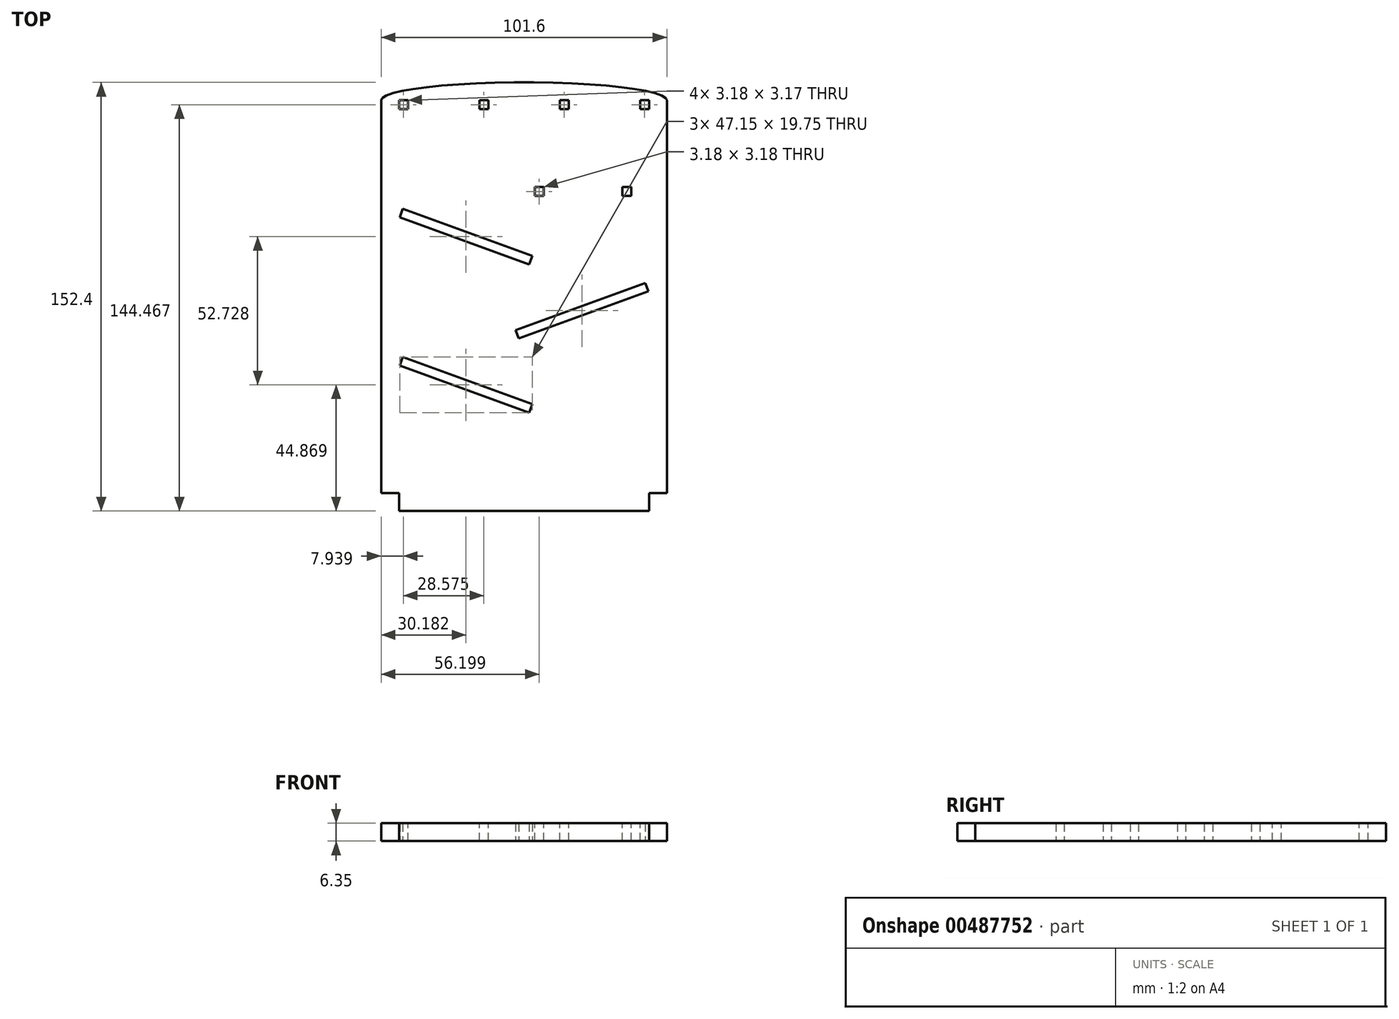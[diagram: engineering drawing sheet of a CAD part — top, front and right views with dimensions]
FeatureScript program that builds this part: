
annotation { "Feature Type Name" : "Feature", "Feature Type Description" : "" }
export const myFeature = defineFeature(function(context is Context, id is Id, definition is map)
    precondition{}
    {
        {
            var Q0;
            Q0=qCreatedBy(makeId("Top.planeOp"),FACE);
            var sketch = newSketch(context, id + "F0", { "sketchPlane" : qUnion([Q0])});
            skLineSegment(sketch, "E0.bottom", {"start": v(-69.59, 73.12) * mm, "end": v(32.01, 73.12) * mm});
            skLineSegment(sketch, "E0.top", {"start": v(-69.59, -72.93) * mm, "end": v(32.01, -72.93) * mm});
            skLineSegment(sketch, "E0.left", {"start": v(-69.59, 73.12) * mm, "end": v(-69.59, -72.93) * mm});
            skLineSegment(sketch, "E0.right", {"start": v(32.01, 73.12) * mm, "end": v(32.01, -72.93) * mm});
            skSolve(sketch);
        }
        {
            var Q0;
            Q0 = qSketchRegion(id + "F0", true);
            extrude(context, id + "F1", {"entities" : qUnion([Q0]), "depth" : 6.35 * mm});
        }
        {
            var Q0;
            Q0=makeQuery(id+"F1.opExtrude","CAP_FACE",FACE,{"disambiguationData":[OSD([sQuery(id+"F0.wireOp",EDGE,"E0.bottom"),sQuery(id+"F0.wireOp",EDGE,"E0.top"),sQuery(id+"F0.wireOp",EDGE,"E0.left"),sQuery(id+"F0.wireOp",EDGE,"E0.right")])],"isStart":false});
            var sketch = newSketch(context, id + "F2", { "sketchPlane" : qUnion([Q0])});
            skPoint(sketch, "E1.oppositeSnap0", {"position": v(-18.79, 73.12) * mm});
            skLineSegment(sketch, "E1.bottom", {"start": v(-69.59, 73.12) * mm, "end": v(-18.79, 73.12) * mm});
            skLineSegment(sketch, "E1.top", {"start": v(-69.59, 79.47) * mm, "end": v(-18.79, 79.47) * mm});
            skLineSegment(sketch, "E1.left", {"start": v(-69.59, 73.12) * mm, "end": v(-69.59, 79.47) * mm});
            skLineSegment(sketch, "E1.right", {"start": v(-18.79, 73.12) * mm, "end": v(-18.79, 79.47) * mm});
            skLineSegment(sketch, "E2.bottom", {"start": v(-18.79, 79.47) * mm, "end": v(32.01, 79.47) * mm});
            skLineSegment(sketch, "E2.top", {"start": v(-18.79, 73.12) * mm, "end": v(32.01, 73.12) * mm});
            skLineSegment(sketch, "E2.left", {"start": v(-18.79, 79.47) * mm, "end": v(-18.79, 73.12) * mm});
            skLineSegment(sketch, "E2.right", {"start": v(32.01, 79.47) * mm, "end": v(32.01, 73.12) * mm});
            skEllipse(sketch, "E3", {"center": v(-18.79, 73.12) * mm, "majorRadius": 50.8 * mm, "minorRadius": 6.35 * mm, "majorAxis": v(-1, 0)});
            skSolve(sketch);
        }
        {
            var Q0;
            {var subQ0=sQuery(id+"F2.wireOp",EDGE,"E1.bottom");Q0=makeQuery(id+"F2.imprint","IMPRINT",FACE,{"disambiguationData":[TD([[makeQuery(id+"F2.imprint","IMPRINT",EDGE,{"derivedFrom":subQ0}),1.0]])]});}
            var Q1;
            {var subQ0=sQuery(id+"F2.wireOp",EDGE,"E2.top");Q1=makeQuery(id+"F2.imprint","IMPRINT",FACE,{"disambiguationData":[TD([[makeQuery(id+"F2.imprint","IMPRINT",EDGE,{"derivedFrom":subQ0}),1.0]])]});}
            extrude(context, id + "F3", {"entities" : qUnion([Q0, Q1]), "operationType" : NewBodyOperationType.ADD, "oppositeDirection" : true, "depth" : 6.35 * mm});
        }
        {
            var Q0;
            Q0=makeQuery(id+"F3.boolean.opBoolean","MERGE",FACE,{"derivedFrom":[makeQuery(id+"F1.opExtrude","CAP_FACE",FACE,{"disambiguationData":[OSD([sQuery(id+"F0.wireOp",EDGE,"E0.bottom"),sQuery(id+"F0.wireOp",EDGE,"E0.top"),sQuery(id+"F0.wireOp",EDGE,"E0.left"),sQuery(id+"F0.wireOp",EDGE,"E0.right")])],"isStart":false}),makeQuery(id+"F3.opExtrude","CAP_FACE",FACE,{"disambiguationData":[OSD([sQuery(id+"F2.wireOp",EDGE,"E1.bottom"),sQuery(id+"F2.wireOp",EDGE,"E2.top"),sQuery(id+"F2.wireOp",EDGE,"E3")])],"isStart":true})]});
            var sketch = newSketch(context, id + "F4", { "sketchPlane" : qUnion([Q0])});
            skLineSegment(sketch, "E4.bottom", {"start": v(-69.59, -72.93) * mm, "end": v(-63.24, -72.93) * mm});
            skLineSegment(sketch, "E4.top", {"start": v(-69.59, -66.58) * mm, "end": v(-63.24, -66.58) * mm});
            skLineSegment(sketch, "E4.left", {"start": v(-69.59, -72.93) * mm, "end": v(-69.59, -66.58) * mm});
            skLineSegment(sketch, "E4.right", {"start": v(-63.24, -72.93) * mm, "end": v(-63.24, -66.58) * mm});
            skLineSegment(sketch, "E5.bottom", {"start": v(32.01, -72.93) * mm, "end": v(25.66, -72.93) * mm});
            skLineSegment(sketch, "E5.top", {"start": v(32.01, -66.58) * mm, "end": v(25.66, -66.58) * mm});
            skLineSegment(sketch, "E5.left", {"start": v(32.01, -72.93) * mm, "end": v(32.01, -66.58) * mm});
            skLineSegment(sketch, "E5.right", {"start": v(25.66, -72.93) * mm, "end": v(25.66, -66.58) * mm});
            skLineSegment(sketch, "E6.bottom", {"start": v(-69.59, 73.12) * mm, "end": v(32.01, 73.12) * mm});
            skLineSegment(sketch, "E6.top", {"start": v(-69.59, 66.77) * mm, "end": v(32.01, 66.77) * mm});
            skLineSegment(sketch, "E6.left", {"start": v(-69.59, 73.12) * mm, "end": v(-69.59, 66.77) * mm});
            skLineSegment(sketch, "E6.right", {"start": v(32.01, 73.12) * mm, "end": v(32.01, 66.77) * mm});
            skLineSegment(sketch, "E7.bottom", {"start": v(-69.59, 66.77) * mm, "end": v(-63.24, 66.77) * mm});
            skLineSegment(sketch, "E8.bottom", {"start": v(32.01, 66.77) * mm, "end": v(25.66, 66.77) * mm});
            skLineSegment(sketch, "E9.bottom", {"start": v(-63.24, 66.77) * mm, "end": v(-69.59, 66.77) * mm});
            skLineSegment(sketch, "E9.top", {"start": v(-63.24, 73.12) * mm, "end": v(-69.59, 73.12) * mm});
            skLineSegment(sketch, "E9.left", {"start": v(-63.24, 66.77) * mm, "end": v(-63.24, 73.12) * mm});
            skLineSegment(sketch, "E9.right", {"start": v(-69.59, 66.77) * mm, "end": v(-69.59, 73.12) * mm});
            skLineSegment(sketch, "E10.bottom", {"start": v(25.66, 66.77) * mm, "end": v(32.01, 66.77) * mm});
            skLineSegment(sketch, "E10.top", {"start": v(25.66, 73.12) * mm, "end": v(32.01, 73.12) * mm});
            skLineSegment(sketch, "E10.left", {"start": v(25.66, 66.77) * mm, "end": v(25.66, 73.12) * mm});
            skLineSegment(sketch, "E10.right", {"start": v(32.01, 66.77) * mm, "end": v(32.01, 73.12) * mm});
            skSolve(sketch);
        }
        {
            var Q0;
            Q0=makeQuery(id+"F4.imprint","IMPRINT",FACE,{"disambiguationData":[TD([[makeQuery(id+"F4.imprint","IMPRINT",EDGE,{"derivedFrom":sQuery(id+"F4.wireOp",EDGE,"E9.bottom")}),-1.0]])]});
            var Q1;
            Q1=makeQuery(id+"F4.imprint","IMPRINT",FACE,{"disambiguationData":[TD([[makeQuery(id+"F4.imprint","IMPRINT",EDGE,{"derivedFrom":sQuery(id+"F4.wireOp",EDGE,"E10.bottom")}),1.0]])]});
            var Q2;
            Q2=makeQuery(id+"F4.imprint","IMPRINT",FACE,{"disambiguationData":[TD([[makeQuery(id+"F4.imprint","IMPRINT",EDGE,{"derivedFrom":sQuery(id+"F4.wireOp",EDGE,"E5.bottom")}),1.0]])]});
            var Q3;
            Q3=makeQuery(id+"F4.imprint","IMPRINT",FACE,{"disambiguationData":[TD([[makeQuery(id+"F4.imprint","IMPRINT",EDGE,{"derivedFrom":sQuery(id+"F4.wireOp",EDGE,"E4.bottom")}),1.0]])]});
            extrude(context, id + "F5", {"entities" : qUnion([Q0, Q1, Q2, Q3]), "operationType" : NewBodyOperationType.REMOVE, "endBound" : BoundingType.THROUGH_ALL, "oppositeDirection" : true, "depth" : 25.4 * mm});
        }
        {
            var Q0;
            Q0=makeQuery(id+"F3.boolean.opBoolean","MERGE",FACE,{"derivedFrom":[makeQuery(id+"F1.opExtrude","CAP_FACE",FACE,{"disambiguationData":[OSD([sQuery(id+"F0.wireOp",EDGE,"E0.bottom"),sQuery(id+"F0.wireOp",EDGE,"E0.top"),sQuery(id+"F0.wireOp",EDGE,"E0.left"),sQuery(id+"F0.wireOp",EDGE,"E0.right")])],"isStart":false}),makeQuery(id+"F3.opExtrude","CAP_FACE",FACE,{"disambiguationData":[OSD([sQuery(id+"F2.wireOp",EDGE,"E1.bottom"),sQuery(id+"F2.wireOp",EDGE,"E2.top"),sQuery(id+"F2.wireOp",EDGE,"E3")])],"isStart":true})]});
            var sketch = newSketch(context, id + "F6", { "sketchPlane" : qUnion([Q0])});
            skLineSegment(sketch, "E11.bottom", {"start": v(-63.24, 73.12) * mm, "end": v(-60.06, 73.12) * mm});
            skLineSegment(sketch, "E11.top", {"start": v(-63.24, 69.95) * mm, "end": v(-60.06, 69.95) * mm});
            skLineSegment(sketch, "E11.left", {"start": v(-63.24, 73.12) * mm, "end": v(-63.24, 69.95) * mm});
            skLineSegment(sketch, "E11.right", {"start": v(-60.06, 73.12) * mm, "end": v(-60.06, 69.95) * mm});
            skLineSegment(sketch, "E12.bottom", {"start": v(-34.66, 73.12) * mm, "end": v(-31.49, 73.12) * mm});
            skLineSegment(sketch, "E12.top", {"start": v(-34.66, 69.95) * mm, "end": v(-31.49, 69.95) * mm});
            skLineSegment(sketch, "E12.left", {"start": v(-34.66, 73.12) * mm, "end": v(-34.66, 69.95) * mm});
            skLineSegment(sketch, "E12.right", {"start": v(-31.49, 73.12) * mm, "end": v(-31.49, 69.95) * mm});
            skLineSegment(sketch, "E13.bottom", {"start": v(-6.09, 73.12) * mm, "end": v(-2.91, 73.12) * mm});
            skLineSegment(sketch, "E13.top", {"start": v(-6.09, 69.95) * mm, "end": v(-2.91, 69.95) * mm});
            skLineSegment(sketch, "E13.left", {"start": v(-6.09, 73.12) * mm, "end": v(-6.09, 69.95) * mm});
            skLineSegment(sketch, "E13.right", {"start": v(-2.91, 73.12) * mm, "end": v(-2.91, 69.95) * mm});
            skLineSegment(sketch, "E14.bottom", {"start": v(22.49, 73.12) * mm, "end": v(25.66, 73.12) * mm});
            skLineSegment(sketch, "E14.top", {"start": v(22.49, 69.95) * mm, "end": v(25.66, 69.95) * mm});
            skLineSegment(sketch, "E14.left", {"start": v(22.49, 73.12) * mm, "end": v(22.49, 69.95) * mm});
            skLineSegment(sketch, "E14.right", {"start": v(25.66, 73.12) * mm, "end": v(25.66, 69.95) * mm});
            skLineSegment(sketch, "E15", {"start": v(-11.8, 42.26) * mm, "end": v(16.14, 42.26) * mm});
            skLineSegment(sketch, "E16.bottom", {"start": v(-11.8, 42.26) * mm, "end": v(-14.98, 42.26) * mm});
            skLineSegment(sketch, "E16.top", {"start": v(-11.8, 39.09) * mm, "end": v(-14.98, 39.09) * mm});
            skLineSegment(sketch, "E16.left", {"start": v(-11.8, 42.26) * mm, "end": v(-11.8, 39.09) * mm});
            skLineSegment(sketch, "E16.right", {"start": v(-14.98, 42.26) * mm, "end": v(-14.98, 39.09) * mm});
            skLineSegment(sketch, "E17.bottom", {"start": v(16.14, 42.26) * mm, "end": v(19.31, 42.26) * mm});
            skLineSegment(sketch, "E17.top", {"start": v(16.14, 39.09) * mm, "end": v(19.31, 39.09) * mm});
            skLineSegment(sketch, "E17.left", {"start": v(16.14, 42.26) * mm, "end": v(16.14, 39.09) * mm});
            skLineSegment(sketch, "E17.right", {"start": v(19.31, 42.26) * mm, "end": v(19.31, 39.09) * mm});
            skLineSegment(sketch, "E18", {"start": v(-63.24, 73.12) * mm, "end": v(25.66, 73.12) * mm});
            skSolve(sketch);
        }
        {
            var Q0;
            Q0=makeQuery(id+"F6.imprint","IMPRINT",FACE,{"disambiguationData":[TD([[makeQuery(id+"F6.imprint","IMPRINT",EDGE,{"derivedFrom":sQuery(id+"F6.wireOp",EDGE,"E11.top")}),1.0]])]});
            var Q1;
            Q1=makeQuery(id+"F6.imprint","IMPRINT",FACE,{"disambiguationData":[TD([[makeQuery(id+"F6.imprint","IMPRINT",EDGE,{"derivedFrom":sQuery(id+"F6.wireOp",EDGE,"E12.top")}),1.0]])]});
            var Q2;
            Q2=makeQuery(id+"F6.imprint","IMPRINT",FACE,{"disambiguationData":[TD([[makeQuery(id+"F6.imprint","IMPRINT",EDGE,{"derivedFrom":sQuery(id+"F6.wireOp",EDGE,"E13.top")}),1.0]])]});
            var Q3;
            Q3=makeQuery(id+"F6.imprint","IMPRINT",FACE,{"disambiguationData":[TD([[makeQuery(id+"F6.imprint","IMPRINT",EDGE,{"derivedFrom":sQuery(id+"F6.wireOp",EDGE,"E14.top")}),1.0]])]});
            var Q4;
            Q4=makeQuery(id+"F6.imprint","IMPRINT",FACE,{"disambiguationData":[TD([[makeQuery(id+"F6.imprint","IMPRINT",EDGE,{"derivedFrom":sQuery(id+"F6.wireOp",EDGE,"E17.bottom")}),-1.0]])]});
            var Q5;
            Q5=makeQuery(id+"F6.imprint","IMPRINT",FACE,{"disambiguationData":[TD([[makeQuery(id+"F6.imprint","IMPRINT",EDGE,{"derivedFrom":sQuery(id+"F6.wireOp",EDGE,"E16.bottom")}),1.0]])]});
            extrude(context, id + "F7", {"entities" : qUnion([Q0, Q1, Q2, Q3, Q4, Q5]), "operationType" : NewBodyOperationType.REMOVE, "endBound" : BoundingType.THROUGH_ALL, "oppositeDirection" : true, "depth" : 25.4 * mm});
        }
        {
            var Q0;
            Q0=qCreatedBy(makeId("Top.planeOp"),FACE);
            var sketch = newSketch(context, id + "F8", { "sketchPlane" : qUnion([Q0])});
            skLineSegment(sketch, "E19", {"start": v(-62.98, 31.56) * mm, "end": v(-16.92, 14.8) * mm});
            skLineSegment(sketch, "E20", {"start": v(-62.98, 31.56) * mm, "end": v(-61.9, 34.54) * mm});
            skLineSegment(sketch, "E21", {"start": v(-61.9, 34.54) * mm, "end": v(-15.83, 17.77) * mm});
            skLineSegment(sketch, "E22", {"start": v(-15.83, 17.77) * mm, "end": v(-16.92, 14.8) * mm});
            skSolve(sketch);
        }
        {
            var Q0;
            Q0 = qSketchRegion(id + "F8", true);
            extrude(context, id + "F9", {"entities" : qUnion([Q0]), "operationType" : NewBodyOperationType.REMOVE, "depth" : 18.29 * mm});
        }
        {
            var Q0;
            Q0=qCreatedBy(makeId("Top.planeOp"),FACE);
            var sketch = newSketch(context, id + "F10", { "sketchPlane" : qUnion([Q0])});
            skLineSegment(sketch, "E23", {"start": v(-21.74, -8.59) * mm, "end": v(24.32, 8.18) * mm});
            skLineSegment(sketch, "E24", {"start": v(24.32, 8.18) * mm, "end": v(25.4, 5.2) * mm});
            skLineSegment(sketch, "E25", {"start": v(25.4, 5.2) * mm, "end": v(-20.66, -11.57) * mm});
            skLineSegment(sketch, "E26", {"start": v(-20.66, -11.57) * mm, "end": v(-21.74, -8.59) * mm});
            skSolve(sketch);
        }
        {
            var Q0;
            Q0 = qSketchRegion(id + "F10", true);
            extrude(context, id + "F11", {"entities" : qUnion([Q0]), "operationType" : NewBodyOperationType.REMOVE, "depth" : 25.65 * mm});
        }
        {
            var Q0;
            Q0=qCreatedBy(makeId("Top.planeOp"),FACE);
            var sketch = newSketch(context, id + "F12", { "sketchPlane" : qUnion([Q0])});
            skLineSegment(sketch, "E27", {"start": v(-61.9, -18.19) * mm, "end": v(-15.83, -34.95) * mm});
            skLineSegment(sketch, "E28", {"start": v(-15.83, -34.95) * mm, "end": v(-16.92, -37.94) * mm});
            skLineSegment(sketch, "E29", {"start": v(-16.92, -37.94) * mm, "end": v(-62.98, -21.17) * mm});
            skLineSegment(sketch, "E30", {"start": v(-62.98, -21.17) * mm, "end": v(-61.9, -18.19) * mm});
            skSolve(sketch);
        }
        {
            var Q0;
            Q0 = qSketchRegion(id + "F12", true);
            extrude(context, id + "F13", {"entities" : qUnion([Q0]), "operationType" : NewBodyOperationType.REMOVE, "depth" : 37.85 * mm});
        }
    });
